# Revit family: LAMP_FIL 35 1400MM OPAL RECESSED
name_source: partatom
category: Luminarias
revit_build: Autodesk Revit 2018 (Build: 20170223_1515(x64)
units: mm (PartAtom-declared; Revit-internal decimal feet)

## family parameters
Anfitrión = Cara
Compartido = No
Corte con vacíos al cargar = No
Cota de conector redondo = Diámetro de uso
Origen de luz = Sí
Punto de cálculo de habitación = No
Tipo de pieza = Normal

## types (12) — shared parameters
CRI = 80
Cambio de temperatura de color de luz atenuada = <Ninguno>
Dimensions = 1400x45x76
Efficacy = 106 lm/W
Elevación por defecto = 1219 mm
Fabricante = LAMP
Filtro de color = 16777215
Gear = Electronic
IEE = A+
Installation instructions = https://www.lamp.es
Insulation class = I
LED Lifetime = 50.000 L90 B10
Lamp = MID-POWER LED
Last update = 04/05/2021
Longitud de línea de emisión = 1400 mm  [stored 4.59318 ft]
MacAdam = 3
Manufacturer URL = http://www.lamp.es
Manufacturer country = Spain
Manufacturer name = LAMP
Material difusor = LAMP_PC Difusor Opal Fil
Material suspension = LAMP_Acero genérico
Plum = 14 W
Power = 14 W
Power Supply = 220-240V 50/60Hz
Product URL = https://www.lamp.es
Product datasheet = http://www.lamp.es
Protection rating = IP20 / IK07
Recessed dimensions = 1408x42x0
Type = MID POWER TRIDONIC
Weight = 3.35 kg
Ángulo de inclinación = -90.00°

## per-type parameters (varying)
| type | Archivo de red fotométrica | Descripción | Finish | Material perfil | Modelo | Product code |
| 1520LM 3000K DALI BLACK | F31RE140LOOP830nB.IES | FIL35 REC 1400 2000 WW OPAL DALI BK. | Matte black RAL 9011 | LAMP_Aluminio Perfil Fil NG | F31RE140LOOP830DB | F31RE140LOOP830DB |
| 1520LM 3000K DALI GREY | F31RE140LOOP830nG.IES | FIL35 REC 1400 2000 WW OPAL DALI GR. | Gloss grey | LAMP_Aluminio Perfil Fil GR | F31RE140LOOP830DG | F31RE140LOOP830DG |
| 1520LM 3000K DALI WHITE | F31RE140LOOP830nW.IES | FIL35 REC 1400 2000 WW OPAL DALI WH. | Matte white RAL 9010 | LAMP_Aluminio Perfil Fil BL | F31RE140LOOP830DW | F31RE140LOOP830DW |
| 1520LM 3000K  BLACK | F31RE140LOOP830NB.IES | FIL35 REC 1400 2000 WW OPAL BK. | Matte black RAL 9011 | LAMP_Aluminio Perfil Fil NG | F31RE140LOOP830NB | F31RE140LOOP830NB |
| 1520LM 3000K  GREY | F31RE140LOOP830NG.IES | FIL35 REC 1400 2000 WW OPAL GR. | Gloss grey | LAMP_Aluminio Perfil Fil GR | F31RE140LOOP830NG | F31RE140LOOP830NG |
| 1520LM 3000K  WHITE | F31RE140LOOP830NW.IES | FIL35 REC 1400 2000 WW OPAL WH. | Matte white RAL 9010 | LAMP_Aluminio Perfil Fil BL | F31RE140LOOP830NW | F31RE140LOOP830NW |
| 1520LM 4000K DALI BLACK | F31RE140LOOP840nB.IES | FIL35 REC 1400 2000 NW OPAL DALI BK. | Matte black RAL 9011 | LAMP_Aluminio Perfil Fil NG | F31RE140LOOP840DB | F31RE140LOOP840DB |
| 1520LM 4000K DALI GREY | F31RE140LOOP840nG.IES | FIL35 REC 1400 2000 NW OPAL DALI GR. | Gloss grey | LAMP_Aluminio Perfil Fil GR | F31RE140LOOP840DG | F31RE140LOOP840DG |
| 1520LM 4000K DALI WHITE | F31RE140LOOP840nW.IES | FIL35 REC 1400 2000 NW OPAL DALI WH. | Matte white RAL 9010 | LAMP_Aluminio Perfil Fil BL | F31RE140LOOP840DW | F31RE140LOOP840DW |
| 1520LM 4000K  BLACK | F31RE140LOOP840NB.IES | FIL35 REC 1400 2000 NW OPAL BK. | Matte black RAL 9011 | LAMP_Aluminio Perfil Fil NG | F31RE140LOOP840NB | F31RE140LOOP840NB |
| 1520LM 4000K  GREY | F31RE140LOOP840NG.IES | FIL35 REC 1400 2000 NW OPAL GR. | Gloss grey | LAMP_Aluminio Perfil Fil GR | F31RE140LOOP840NG | F31RE140LOOP840NG |
| 1520LM 4000K  WHITE | F31RE140LOOP840NW.IES | FIL35 REC 1400 2000 NW OPAL WH. | Matte white RAL 9010 | LAMP_Aluminio Perfil Fil BL | F31RE140LOOP840NW | F31RE140LOOP840NW |

note: [stored X ft] marks values corroborated as IEEE doubles in the binary element streams (Revit-internal decimal feet)
